# Revit family: IS_iLifeA_T4517_BIM_GB
name_source: partatom
category: Plumbing Fixtures
units: mm (PartAtom-declared; Revit-internal decimal feet)

## family parameters
Always vertical = No
Cut with Voids When Loaded = Yes
OmniClass Number = 23.45.05.14.14
OmniClass Title = Sinks/Lavatories
Part Type = Normal
Room Calculation Point = No
Round Connector Dimension = Use Diameter
Shared = No
Work Plane-Based = No

## types (2) — shared parameters
Accessories = https://www.idealstandard.co.uk
AreaUnits = millimetres
AssetType = fixed
BIMObjectName = IS_IdealStandard_Wall-hunghandrinsebasins_i.lifeA_T4517
BIMobject category = Wash Basins
BIMobject category code = wash-basins
BIMobject main category = Sanitary
BIMobject main category code = sanitary
BarCode = 8014140485858
Brand = Ideal Standard
Brand url = http://www.idealstandard.co.uk
ConnectionType = Plumbing
CurrencyUnit = £
CurrentRevision = 1
Date of publishing = 07/10/2022
DurationUnit = years
Edition number = 1
ElementType = fixed
ExpectedLife = 99
GTIN code = https://8014140485858
Help = https://www.idealstandard.co.uk
IFC Classification = Sanitary Terminal
IfcExportAs = IfcSanitaryTerminalType
IfcExportType = WASHHANDBASIN
Installation instructions = https://www.idealstandard.co.uk
InstallationDate = n /a
InstallationInstructions = https://www.idealstandard.co.uk
LinearUnits = millimetres
MainColor = White
MaintenanceInformation = https://www.idealstandard.co.uk
Manufacturer = Ideal Standard
Manufacturer name = Ideal Standard
ManufacturerURL = https://www.idealstandard.co.uk
Masterformat 2014 Code = 22 40 00
Masterformat 2014 Description = Plumbing Fixtures
Material = Ceramics
Material main = Ceramics
NBS Reference Code = 45-35-70/369
NBS Reference Description = Wall hung wash basins
Name = Wall-hunghandrinsebasins_i.lifeA_T4517_IdealStandard
NettWeight = 11.82
NominalDepth = 440 mm
NominalHeight = 170 mm
NominalWidth = 501 mm
OmniClass Code = 23-39 13 21 19
OmniClass Description = Surface Water Retention Basins
Product Guid = 06699d95-075b-40d6-bf1e-4ce8c1a50cda
Product SKU = T4517
Product certification = https://www.idealstandard.co.uk
Product data url = https://bimobject.com
Product family = I.life A
Product group = Basin
Product name = IDEAL STANDARD I.LIFE A , SEMICOUNTERTOP 50 CM,  WITH CENTER TAPHOLE, WITH OVERFLOW
Product url = https://www.idealstandard.co.uk
ProductInformation = https://www.idealstandard.co.uk
QR code = http://bimobject.com
Shape = sculptured
Size = 501 x 440 x 170 mm
Space = Internal
SpareParts = https://www.idealstandard.co.uk
Technical description = https://www.idealstandard.co.uk
UNSPSC Code = 301815
URL = https://www.idealstandard.co.uk
Uniclass 1.4 Code = L7212
Uniclass 1.4 Description = Washbasins
Uniclass 2.0 Code = Pr_40_30_79_95
Uniclass 2.0 Description = Wall-Hung Hand Rinse Basins
Uniclass 2015 Code = Pr_40_20_96_95
Uniclass 2015 Name = Wall-hung hand rinse basins
Uniclass2015Code = Pr_40_20_96_95
Uniclass2015Title = Wall-hung hand rinse basins
Uniclass2015Version = v1.27
Uniformat II Code = D2010
Uniformat II Description = Plumbing Fixtures
Version = 1
VolumeUnits = liters
WRASURL = https://www.wrasapprovals.co.uk
WarrantyDescription = manufacturer warranty
WarrantyDurationUnit = years
WashHandBasinMounting = semicountertop
WashHandBasinType = semicountertop
Weight Net (Kg) = 11.82
Youtube clip = https://www.wrasapprovals.co.uk

## per-type parameters (varying)
| type | Color | Description | Features | Finish | Model | ModelNumber | ModelReference |
| T451701 - Ideal Standard i.life A , semicountertop 50 cm,  with center taphole, overflow | White | Semicountertop 50 cm,  with center taphole, overflow | Semicountertop 50 cm,  with center taphole, overflow | White | T451701 | T451701 | I.life A Semicountertop 50 cm,  with center taphole, overflow |
| T4517MA - Ideal Standard i.life A , semicountertop 50 cm,  with center taphole, overflow, white Ideal Plus | White Ideal Plus | Semicountertop 50 cm,  with center taphole, overflow, white Ideal Plus | Semicountertop 50 cm,  with center taphole, overflow, white Ideal Plus | White Ideal Plus | T4517MA | T4517MA | I.life A Semicountertop 50 cm,  with center taphole, overflow, white Ideal Plus |

## geometry (parser evidence)
native form markers: Sweep x1
no freeform markers — native parametric forms only
